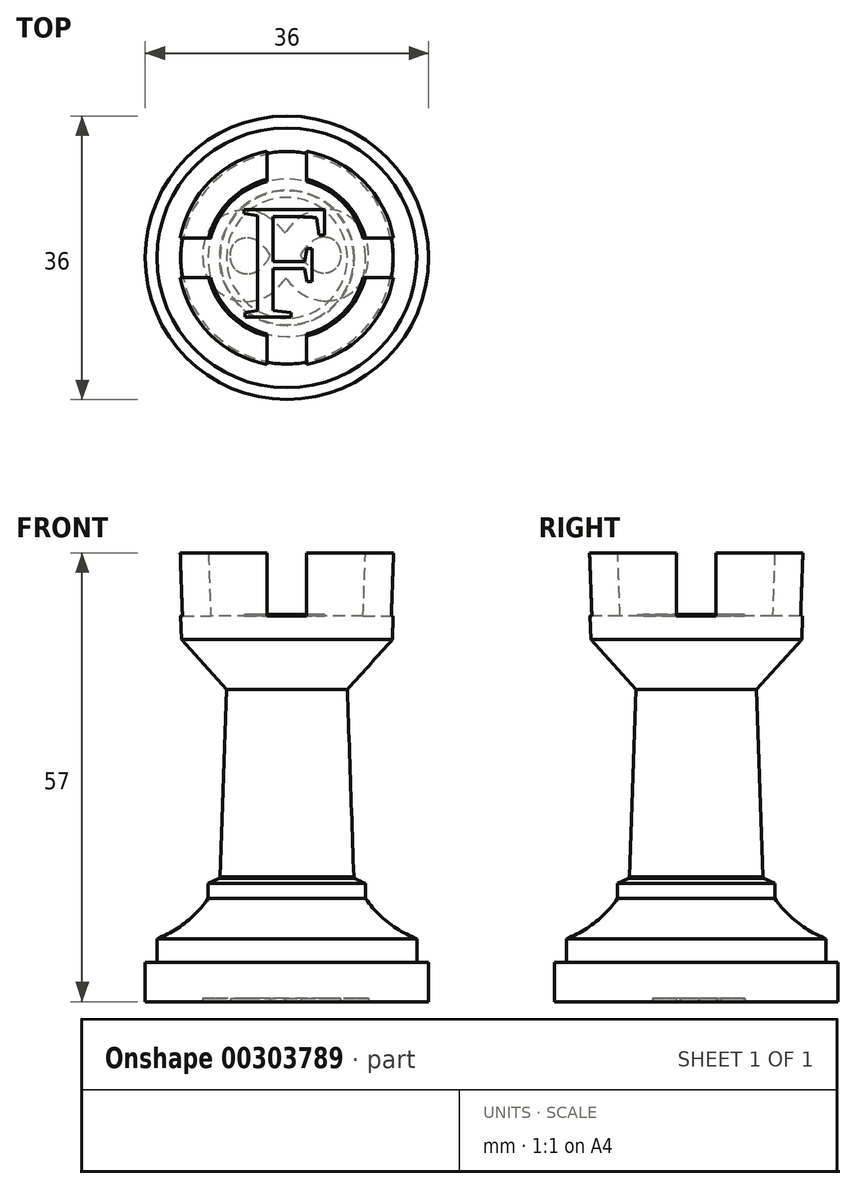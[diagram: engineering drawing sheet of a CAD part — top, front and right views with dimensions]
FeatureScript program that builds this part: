
annotation { "Feature Type Name" : "Feature", "Feature Type Description" : "" }
export const myFeature = defineFeature(function(context is Context, id is Id, definition is map)
    precondition{}
    {
        {
            var Q0;
            Q0=qCreatedBy(makeId("Front.planeOp"),FACE);
            var sketch = newSketch(context, id + "F0", { "sketchPlane" : qUnion([Q0])});
            skLineSegment(sketch, "E0", {"start": v(0, 0) * mm, "end": v(16.5, 0) * mm, "construction": true});
            skLineSegment(sketch, "E1", {"start": v(16.5, 0) * mm, "end": v(16.5, 3) * mm});
            skLineSegment(sketch, "E2", {"start": v(10, 44) * mm, "end": v(0, 44) * mm, "construction": true});
            skLineSegment(sketch, "E3", {"start": v(0, 44) * mm, "end": v(0, 0) * mm});
            skPoint(sketch, "E4.visualSharp", {"position": v(8.5, 3) * mm});
            skArc(sketch, "E4.filletArc", {"start": v(8.5, 10.88) * mm, "mid": v(8.55, 10.77) * mm, "end": v(8.6, 10.66) * mm});
            skLineSegment(sketch, "E5", {"start": v(10.28, 52) * mm, "end": v(10, 44) * mm});
            skLineSegment(sketch, "E6", {"start": v(10, 44) * mm, "end": v(0, 44) * mm});
            skLineSegment(sketch, "E7", {"start": v(0, 0) * mm, "end": v(0, -5) * mm});
            skLineSegment(sketch, "E8", {"start": v(0, -5) * mm, "end": v(18, -5) * mm});
            skLineSegment(sketch, "E9", {"start": v(18, -5) * mm, "end": v(18, 0) * mm});
            skLineSegment(sketch, "E10", {"start": v(18, 0) * mm, "end": v(16.5, 0) * mm});
            skLineSegment(sketch, "E11", {"start": v(10, 8.1) * mm, "end": v(10, 10) * mm});
            skLineSegment(sketch, "E12", {"start": v(10, 10) * mm, "end": v(8.6, 10.66) * mm});
            skArc(sketch, "E13.trimOffspring", {"start": v(10, 8.1) * mm, "mid": v(12.87, 5.06) * mm, "end": v(16.5, 3) * mm});
            skLineSegment(sketch, "E14", {"start": v(13.78, 52) * mm, "end": v(10.28, 52) * mm});
            skPoint(sketch, "E15.orphan", {"position": v(7.5, 44) * mm});
            skLineSegment(sketch, "E16", {"start": v(8.5, 10.88) * mm, "end": v(7.67, 34.64) * mm});
            skLineSegment(sketch, "E17", {"start": v(13.78, 52) * mm, "end": v(13.4, 41) * mm});
            skLineSegment(sketch, "E18", {"start": v(13.4, 41) * mm, "end": v(7.67, 34.64) * mm});
            skSolve(sketch);
        }
        {
            var Q0;
            Q0 = qSketchRegion(id + "F0", true);
            var Q1;
            Q1=sQuery(id+"F0.wireOp",EDGE,"E3");
            revolve(context, id + "F1", {"entities" : qUnion([Q0]), "axis" : qUnion([Q1]), "revolveType" : RevolveType.FULL});
        }
        {
            var Q0;
            Q0=makeQuery(id+"F1.opRevolve","SWEPT_FACE",FACE,{"disambiguationData":[OSD([sQuery(id+"F0.wireOp",EDGE,"E6")])]});
            var sketch = newSketch(context, id + "F2", { "sketchPlane" : qUnion([Q0])});
            skLineSegment(sketch, "E19.bottom", {"start": v(-18.1, 2.5) * mm, "end": v(19.23, 2.5) * mm});
            skLineSegment(sketch, "E19.top", {"start": v(-18.1, -2.5) * mm, "end": v(19.23, -2.5) * mm});
            skLineSegment(sketch, "E19.left", {"start": v(-18.1, 2.5) * mm, "end": v(-18.1, -2.5) * mm});
            skLineSegment(sketch, "E19.right", {"start": v(19.23, 2.5) * mm, "end": v(19.23, -2.5) * mm});
            skLineSegment(sketch, "E20.bottom", {"start": v(-2.5, 18.32) * mm, "end": v(2.5, 18.32) * mm});
            skLineSegment(sketch, "E20.top", {"start": v(-2.5, -18.5) * mm, "end": v(2.5, -18.5) * mm});
            skLineSegment(sketch, "E20.left", {"start": v(-2.5, 18.32) * mm, "end": v(-2.5, -18.5) * mm});
            skLineSegment(sketch, "E20.right", {"start": v(2.5, 18.32) * mm, "end": v(2.5, -18.5) * mm});
            skSolve(sketch);
        }
        {
            var Q0;
            Q0 = qSketchRegion(id + "F2", true);
            extrude(context, id + "F3", {"entities" : qUnion([Q0]), "operationType" : NewBodyOperationType.REMOVE, "endBound" : BoundingType.THROUGH_ALL, "depth" : 25 * mm});
        }
        {
            var Q0;
            Q0=makeQuery(id+"F3.boolean.opBoolean","MERGE",FACE,{"derivedFrom":[makeQuery(id+"F1.opRevolve","SWEPT_FACE",FACE,{"disambiguationData":[OSD([sQuery(id+"F0.wireOp",EDGE,"E6")])]}),makeQuery(id+"F3.opExtrude","CAP_FACE",FACE,{"disambiguationData":[OSD([sQuery(id+"F2.wireOp",EDGE,"E19.bottom"),sQuery(id+"F2.wireOp",EDGE,"E19.top"),sQuery(id+"F2.wireOp",EDGE,"E19.left"),sQuery(id+"F2.wireOp",EDGE,"E19.right"),sQuery(id+"F2.wireOp",EDGE,"E20.bottom"),sQuery(id+"F2.wireOp",EDGE,"E20.top"),sQuery(id+"F2.wireOp",EDGE,"E20.left"),sQuery(id+"F2.wireOp",EDGE,"E20.right")])],"isStart":true})]});
            var sketch = newSketch(context, id + "F4", { "sketchPlane" : qUnion([Q0])});
            skText(sketch, "E21", { "text": "F", "fontName": "Tinos-Regular.ttf"});
            skLineSegment(sketch, "E22", {"start": v(-6.07, 7.5) * mm, "end": v(6.07, -7.5) * mm, "construction": true});
            const initialGuessF4  = {"E21": [-0.00607, -0.0075, 1, 0, 0.015]};
            skSetInitialGuess(sketch, initialGuessF4);
            skSolve(sketch);
        }
        {
            var Q0;
            Q0 = qSketchRegion(id + "F4", true);
            extrude(context, id + "F5", {"entities" : qUnion([Q0]), "operationType" : NewBodyOperationType.ADD, "depth" : .2 * mm});
        }
        {
            var Q0;
            Q0=makeQuery(id+"F1.opRevolve","SWEPT_FACE",FACE,{"disambiguationData":[OSD([sQuery(id+"F0.wireOp",EDGE,"E8")])]});
            var sketch = newSketch(context, id + "F6", { "sketchPlane" : qUnion([Q0])});
            skText(sketch, "E23", { "text": "∞", "fontName": "OpenSans-Bold.ttf"});
            skLineSegment(sketch, "E24", {"start": v(-12.64, 12.7) * mm, "end": v(12.64, -12.7) * mm, "construction": true});
            const initialGuessF6  = {"E23": [-0.01264, -0.0127, 1, 0, 0.0254]};
            skSetInitialGuess(sketch, initialGuessF6);
            skSolve(sketch);
        }
        {
            var Q0;
            Q0 = qSketchRegion(id + "F6", true);
            extrude(context, id + "F7", {"entities" : qUnion([Q0]), "operationType" : NewBodyOperationType.REMOVE, "oppositeDirection" : true, "depth" : .4 * mm});
        }
    });
